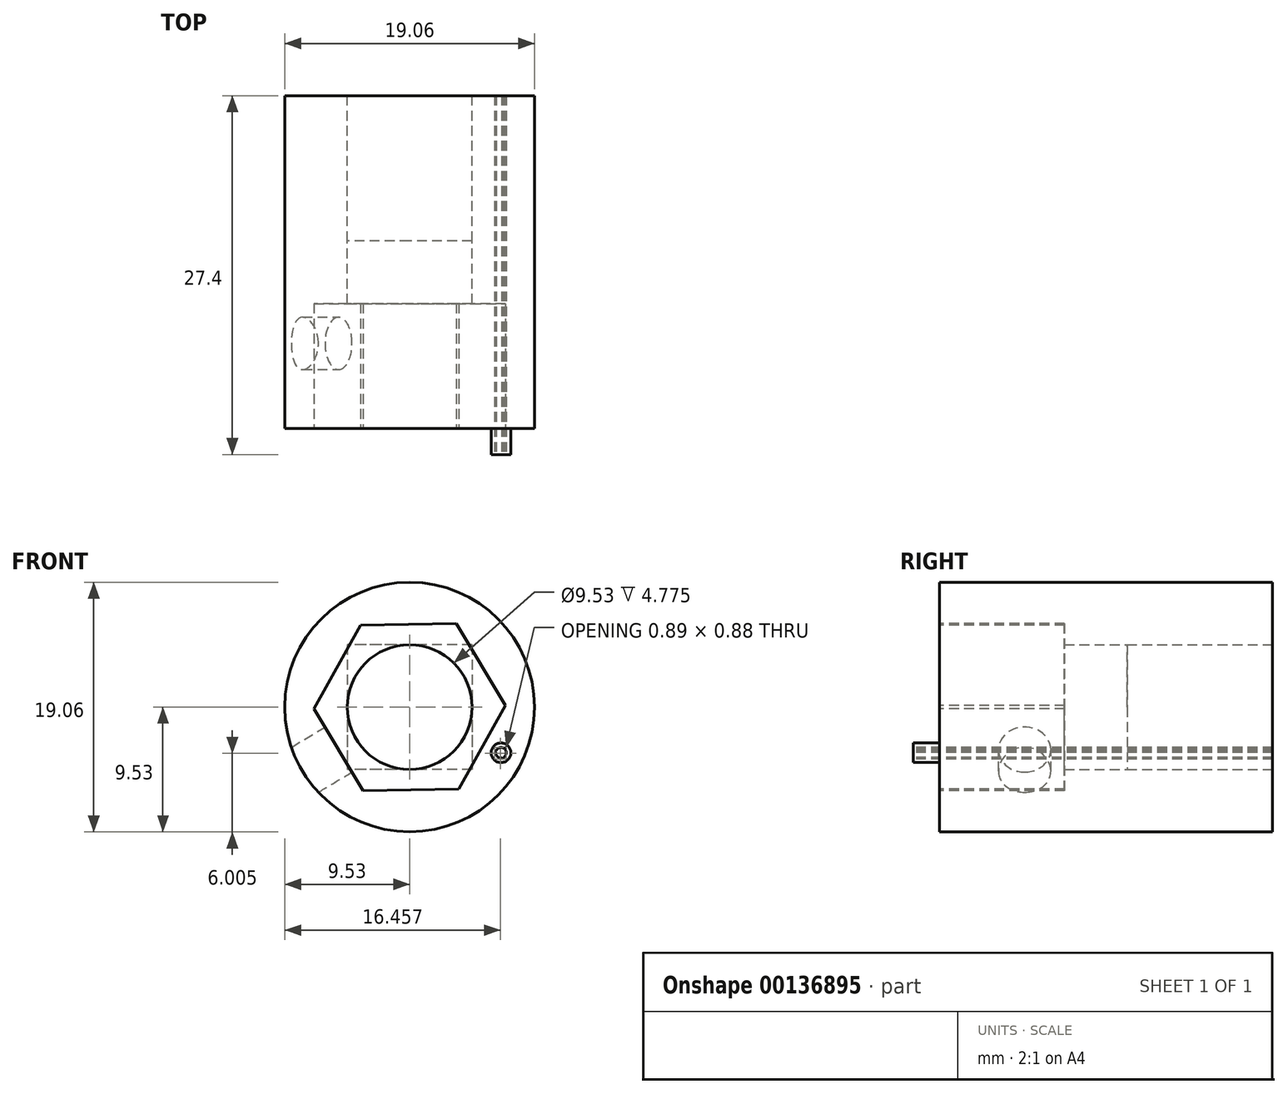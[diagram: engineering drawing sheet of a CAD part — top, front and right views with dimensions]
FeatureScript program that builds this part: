
annotation { "Feature Type Name" : "Feature", "Feature Type Description" : "" }
export const myFeature = defineFeature(function(context is Context, id is Id, definition is map)
    precondition{}
    {
        {
            var Q0;
            Q0=qCreatedBy(makeId("Front.planeOp"),FACE);
            var sketch = newSketch(context, id + "F0", { "sketchPlane" : qUnion([Q0])});
            skCircle(sketch, "E0", {"center": v(0, 0) * mm, "radius": 9.53 * mm});
            skSolve(sketch);
        }
        {
            var Q0;
            Q0 = qSketchRegion(id + "F0", true);
            extrude(context, id + "F1", {"entities" : qUnion([Q0]), "depth" : 25.4 * mm});
        }
        {
            var Q0;
            Q0=qCreatedBy(makeId("Front.planeOp"),FACE);
            var sketch = newSketch(context, id + "F2", { "sketchPlane" : qUnion([Q0])});
            skLineSegment(sketch, "E1.bottom", {"start": v(4.76, 4.76) * mm, "end": v(-4.76, 4.76) * mm});
            skLineSegment(sketch, "E1.top", {"start": v(4.76, -4.76) * mm, "end": v(-4.76, -4.76) * mm});
            skLineSegment(sketch, "E1.left", {"start": v(4.76, 4.76) * mm, "end": v(4.76, -4.76) * mm});
            skLineSegment(sketch, "E1.right", {"start": v(-4.76, 4.76) * mm, "end": v(-4.76, -4.76) * mm});
            skPoint(sketch, "E1.middle", {"position": v(0, 0) * mm});
            skCircle(sketch, "E2", {"center": v(0, 0) * mm, "radius": 4.76 * mm});
            skSolve(sketch);
        }
        {
            var Q0;
            {var subQ0=sQuery(id+"F2.wireOp",EDGE,"E2");var subQ1=makeQuery(id+"F2.imprint","INTERSECT",VERTEX,{"derivedFrom":[sQuery(id+"F2.wireOp",EDGE,"E1.bottom"),subQ0]});Q0=makeQuery(id+"F2.imprint","IMPRINT",FACE,{"disambiguationData":[TD([[makeQuery(id+"F2.imprint","IMPRINT",EDGE,{"disambiguationData":[TD([[subQ1,1.0]])],"derivedFrom":subQ0}),1.0]])]});}
            var Q1;
            Q1=sQuery(id+"F2.wireOp",EDGE,"E2");
            extrude(context, id + "F3", {"entities" : qUnion([Q0]), "operationType" : NewBodyOperationType.REMOVE, "surfaceEntities" : qUnion([Q1]), "endBound" : BoundingType.THROUGH_ALL, "depth" : 25.4 * mm});
        }
        {
            var Q0;
            Q0 = qSketchRegion(id + "F2", true);
            extrude(context, id + "F4", {"entities" : qUnion([Q0]), "operationType" : NewBodyOperationType.REMOVE, "depth" : 11.1 * mm});
        }
        {
            var Q0;
            Q0=makeQuery(id+"F1.opExtrude","CAP_FACE",FACE,{"disambiguationData":[OSD([sQuery(id+"F0.wireOp",EDGE,"E0")])],"isStart":false});
            var sketch = newSketch(context, id + "F5", { "sketchPlane" : qUnion([Q0])});
            skCircle(sketch, "E3.cCircle", {"center": v(0, 0) * mm, "radius": 6.32 * mm, "construction": true});
            skLineSegment(sketch, "E3.0", {"start": v(3.55, 6.38) * mm, "end": v(7.3, 0.12) * mm});
            skLineSegment(sketch, "E3.1", {"start": v(7.3, 0.12) * mm, "end": v(3.75, -6.27) * mm});
            skLineSegment(sketch, "E3.2", {"start": v(3.75, -6.27) * mm, "end": v(-3.55, -6.38) * mm});
            skLineSegment(sketch, "E3.3", {"start": v(-3.55, -6.38) * mm, "end": v(-7.3, -0.12) * mm});
            skLineSegment(sketch, "E3.4", {"start": v(-7.3, -0.12) * mm, "end": v(-3.75, 6.27) * mm});
            skLineSegment(sketch, "E3.5", {"start": v(-3.75, 6.27) * mm, "end": v(3.55, 6.38) * mm});
            skPoint(sketch, "E3.0.midPoint", {"position": v(5.43, 3.25) * mm});
            skSolve(sketch);
        }
        {
            var Q0;
            Q0=makeQuery(id+"F5.imprint","IMPRINT",FACE,{"disambiguationData":[TD([[makeQuery(id+"F5.imprint","IMPRINT",EDGE,{"derivedFrom":sQuery(id+"F5.wireOp",EDGE,"E3.0")}),-1.0]])]});
            extrude(context, id + "F6", {"entities" : qUnion([Q0]), "operationType" : NewBodyOperationType.REMOVE, "oppositeDirection" : true, "depth" : 9.52 * mm});
        }
        {
            var Q0;
            Q0=makeQuery(id+"F1.opExtrude","CAP_FACE",FACE,{"disambiguationData":[OSD([sQuery(id+"F0.wireOp",EDGE,"E0")])],"isStart":false});
            var sketch = newSketch(context, id + "F7", { "sketchPlane" : qUnion([Q0])});
            skCircle(sketch, "E4", {"center": v(6.97, -3.49) * mm, "radius": 0.75 * mm});
            skSolve(sketch);
        }
        {
            var Q0;
            Q0 = qSketchRegion(id + "F7", true);
            extrude(context, id + "F8", {"entities" : qUnion([Q0]), "operationType" : NewBodyOperationType.ADD, "depth" : 2 * mm});
        }
        {
            var Q0;
            Q0=makeQuery(id+"F8.opExtrude","CAP_FACE",FACE,{"disambiguationData":[OSD([sQuery(id+"F7.wireOp",EDGE,"E4")])],"isStart":false});
            var sketch = newSketch(context, id + "F9", { "sketchPlane" : qUnion([Q0])});
            skCircle(sketch, "E5.cCircle", {"center": v(6.97, -3.49) * mm, "radius": 0.5 * mm, "construction": true});
            skLineSegment(sketch, "E5.0", {"start": v(7.31, -3.12) * mm, "end": v(7.12, -3.96) * mm});
            skLineSegment(sketch, "E5.1", {"start": v(7.12, -3.96) * mm, "end": v(6.48, -3.37) * mm});
            skLineSegment(sketch, "E5.2", {"start": v(6.48, -3.37) * mm, "end": v(7.31, -3.12) * mm});
            skSolve(sketch);
        }
        {
            var Q0;
            Q0=makeQuery(id+"F9.imprint","IMPRINT",FACE,{"disambiguationData":[TD([[makeQuery(id+"F9.imprint","IMPRINT",EDGE,{"derivedFrom":sQuery(id+"F9.wireOp",EDGE,"E5.0")}),-1.0]])]});
            extrude(context, id + "F10", {"entities" : qUnion([Q0]), "operationType" : NewBodyOperationType.REMOVE, "endBound" : BoundingType.THROUGH_ALL, "oppositeDirection" : true, "depth" : 25 * mm});
        }
        {
            var Q0;
            Q0=sQuery(id+"F9.wireOp",VERTEX,"E5.cCircle.center");
            var Q1;
            Q1=makeQuery(id+"F1.opExtrude","SWEPT_BODY",BODY,{"disambiguationData":[OSD([sQuery(id+"F0.wireOp",EDGE,"E0")])]});
            hole(context, id + "F11", {"style" : HoleStyle.SIMPLE, "endStyle" : HoleEndStyle.THROUGH, "holeDiameter" : .8 * mm, "locations" : qUnion([Q0]), "scope" : qUnion([Q1]), "isTappedThrough" : true});
        }
        {
            var Q0;
            Q0=makeQuery(id+"F6.boolean.opBoolean","COPY",FACE,{"derivedFrom":makeQuery(id+"F6.opExtrude","SWEPT_FACE",FACE,{"disambiguationData":[OSD([sQuery(id+"F5.wireOp",EDGE,"E3.3")])]})});
            var sketch = newSketch(context, id + "F12", { "sketchPlane" : qUnion([Q0])});
            skCircle(sketch, "E6", {"center": v(-18.91, 0) * mm, "radius": 2 * mm});
            skSolve(sketch);
        }
        {
            var Q0;
            Q0=makeQuery(id+"F12.imprint","IMPRINT",FACE,{"disambiguationData":[TD([[makeQuery(id+"F12.imprint","IMPRINT",EDGE,{"derivedFrom":sQuery(id+"F12.wireOp",EDGE,"E6")}),1.0]])]});
            extrude(context, id + "F13", {"entities" : qUnion([Q0]), "operationType" : NewBodyOperationType.REMOVE, "oppositeDirection" : true, "depth" : 25 * mm});
        }
    });
